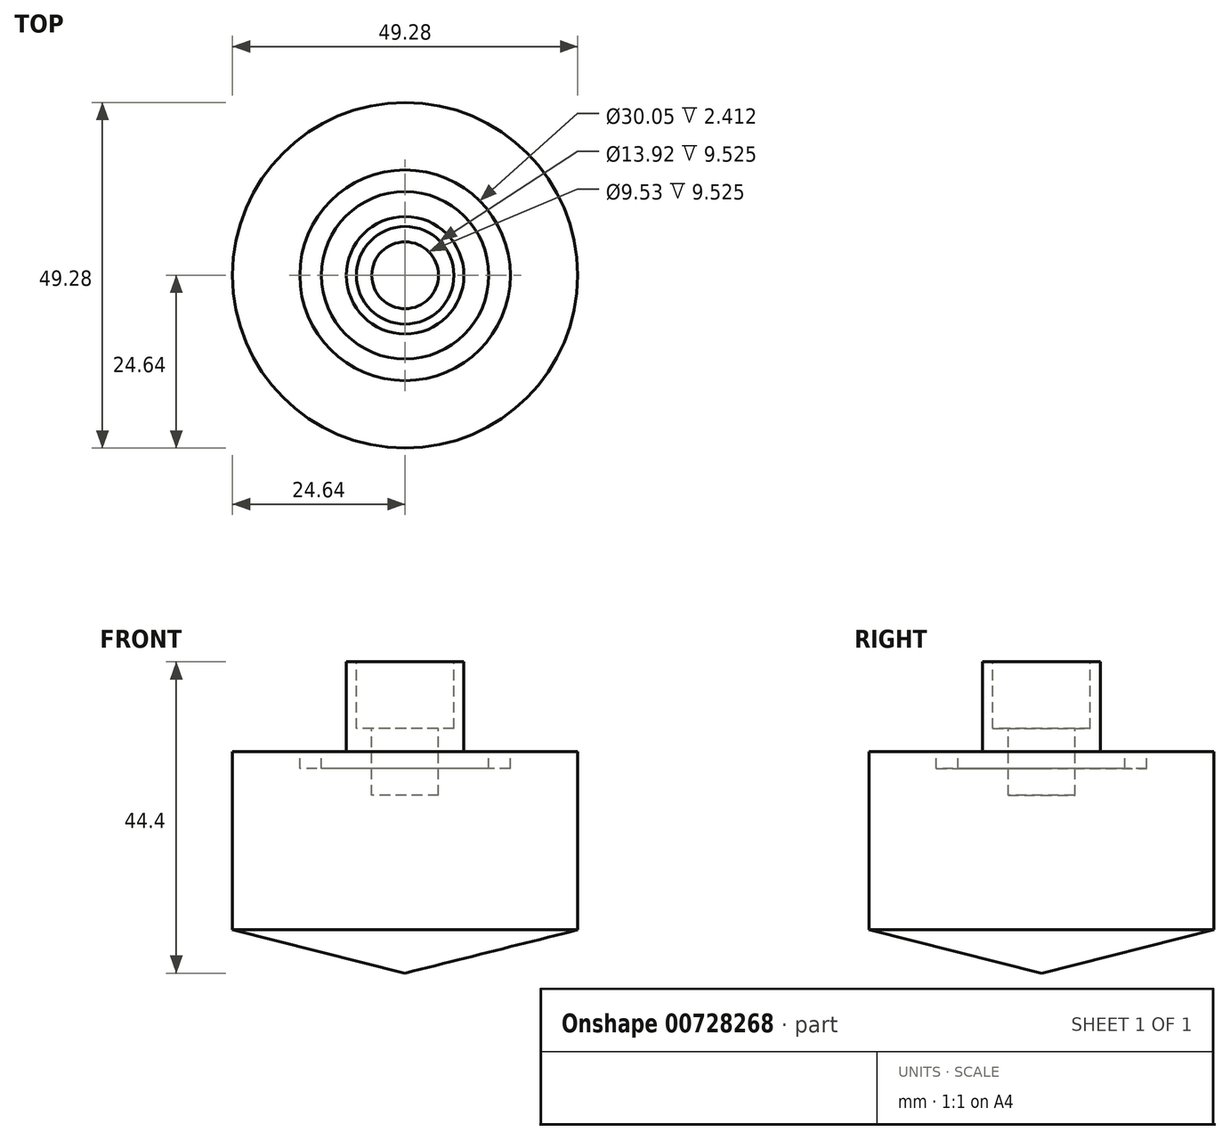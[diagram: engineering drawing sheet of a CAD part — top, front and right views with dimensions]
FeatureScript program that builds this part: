
annotation { "Feature Type Name" : "Feature", "Feature Type Description" : "" }
export const myFeature = defineFeature(function(context is Context, id is Id, definition is map)
    precondition{}
    {
        {
            var Q0;
            Q0=qCreatedBy(makeId("Front.planeOp"),FACE);
            var sketch = newSketch(context, id + "F0", { "sketchPlane" : qUnion([Q0])});
            skLineSegment(sketch, "E0", {"start": v(0, 0) * mm, "end": v(24.64, 6.17) * mm});
            skLineSegment(sketch, "E1", {"start": v(24.64, 6.17) * mm, "end": v(24.64, 31.57) * mm});
            skLineSegment(sketch, "E2", {"start": v(24.64, 31.57) * mm, "end": v(15.02, 31.57) * mm});
            skLineSegment(sketch, "E3", {"start": v(8.38, 31.57) * mm, "end": v(8.38, 44.4) * mm});
            skLineSegment(sketch, "E4", {"start": v(8.38, 44.4) * mm, "end": v(0, 44.4) * mm});
            skLineSegment(sketch, "E5", {"start": v(0, 44.4) * mm, "end": v(0, 0) * mm});
            skLineSegment(sketch, "E6", {"start": v(11.94, 31.57) * mm, "end": v(8.38, 31.57) * mm});
            skPoint(sketch, "E7.end.orphan", {"position": v(11.94, 29.16) * mm});
            skLineSegment(sketch, "E8", {"start": v(11.94, 31.57) * mm, "end": v(11.94, 29.16) * mm});
            skLineSegment(sketch, "E9", {"start": v(15.02, 29.16) * mm, "end": v(15.02, 31.57) * mm});
            skLineSegment(sketch, "E10", {"start": v(11.94, 29.16) * mm, "end": v(15.02, 29.16) * mm});
            skSolve(sketch);
        }
        {
            var Q0;
            Q0=makeQuery(id+"F0.imprint","IMPRINT",FACE,{"disambiguationData":[TD([[makeQuery(id+"F0.imprint","IMPRINT",EDGE,{"derivedFrom":sQuery(id+"F0.wireOp",EDGE,"E0")}),1.0]])]});
            var Q1;
            Q1=sQuery(id+"F0.wireOp",EDGE,"E5");
            revolve(context, id + "F1", {"surfaceOperationType" : NewSurfaceOperationType.NEW, "entities" : qUnion([Q0]), "axis" : qUnion([Q1]), "revolveType" : RevolveType.FULL});
        }
        {
            var Q0;
            Q0=makeQuery(id+"F1.opRevolve","SWEPT_FACE",FACE,{"disambiguationData":[OSD([sQuery(id+"F0.wireOp",EDGE,"E4")])]});
            var sketch = newSketch(context, id + "F2", { "sketchPlane" : qUnion([Q0])});
            skCircle(sketch, "E11", {"center": v(0, 0) * mm, "radius": 4.76 * mm});
            skCircle(sketch, "E12", {"center": v(0, 0) * mm, "radius": 6.96 * mm});
            skSolve(sketch);
        }
        {
            var Q0;
            Q0 = qSketchRegion(id + "F2", true);
            extrude(context, id + "F3", {"entities" : qUnion([Q0]), "operationType" : NewBodyOperationType.REMOVE, "oppositeDirection" : true, "depth" : 9.52 * mm, "offsetDistance" : 25.4 * mm});
        }
        {
            var Q0;
            Q0=makeQuery(id+"F3.boolean.opBoolean","SPLIT",FACE,{"disambiguationData":[TD([makeQuery(id+"F3.opExtrude","SWEPT_FACE",FACE,{"disambiguationData":[OSD([sQuery(id+"F2.wireOp",EDGE,"E11")])]})])],"derivedFrom":makeQuery(id+"F1.opRevolve","SWEPT_FACE",FACE,{"disambiguationData":[OSD([sQuery(id+"F0.wireOp",EDGE,"E4")])]})});
            extrude(context, id + "F4", {"entities" : qUnion([Q0]), "operationType" : NewBodyOperationType.REMOVE, "oppositeDirection" : true, "depth" : 19.05 * mm, "offsetDistance" : 25.4 * mm});
        }
    });
